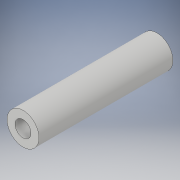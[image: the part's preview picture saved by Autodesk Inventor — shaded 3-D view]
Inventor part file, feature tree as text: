
AUTODESK INVENTOR PART (.ipt)
format: ipt  version: 2019.1 (Build 231200000, 200)  size: 95,232 bytes
history: native  units: in
note: dims shown in document units (in); Inventor stores cm internally (conversion verified against a paired STEP export)
features: extrude x1, sketch x1
ambient origin geometry x8: Origin, YZ Plane, XZ Plane, XY Plane, X Axis, Y Axis, Z Axis, Center Point
bodies: Solid1 (feature_tree)
feature tree (2):
  extrude  "Extrusion1"  Depth=0.125in
  sketch  "Sketch1"  dims[d0=0.25in d1=0.125in d2=1.05in d3=0.0in]
